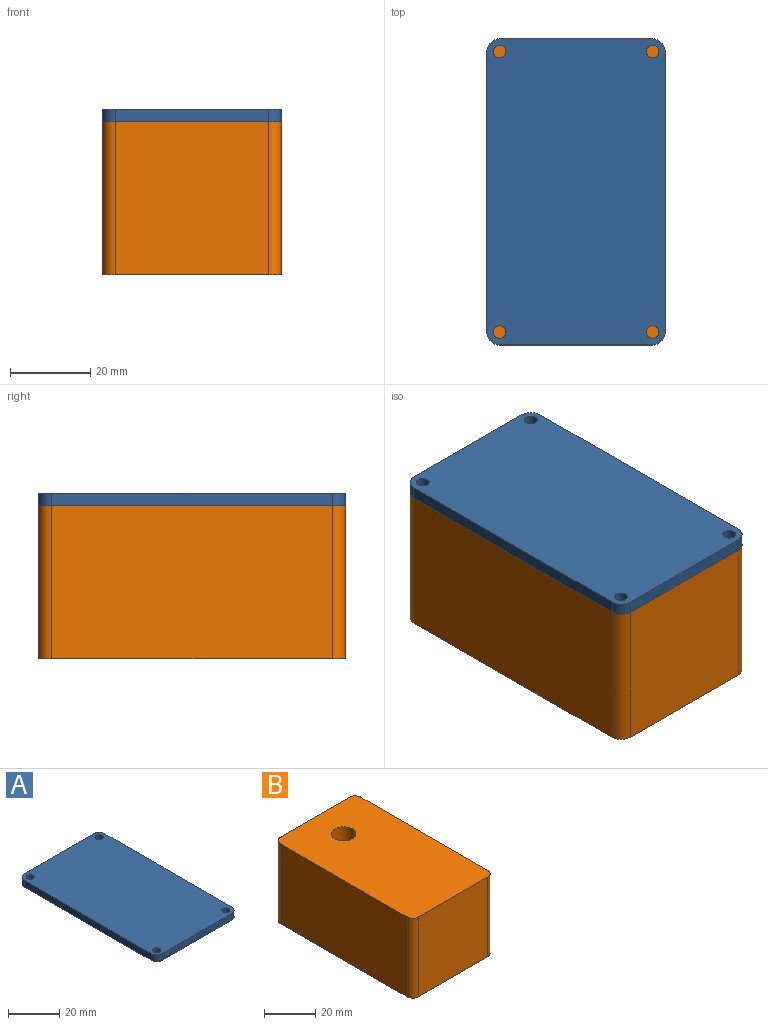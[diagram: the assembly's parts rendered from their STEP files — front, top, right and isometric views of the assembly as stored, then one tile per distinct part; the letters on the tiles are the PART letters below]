
ASSEMBLY  parts=2 mates=1
PART A: 14 faces, bbox 44.5x76.2x3.2 mm
  f0: plane 69.85x3.18mm, normal (1,0,0), area 221.8mm2, adj f1,f7,f8,f9
  f1: cylinder r=3.17mm len=3.18mm, axis (0,0,-1), area 15.8mm2, adj f0,f2,f8,f9
  f2: plane 38.1x3.18mm, normal (0,1,0), area 121mm2, adj f1,f3,f8,f9
  f3: cylinder r=3.17mm len=3.18mm, axis (0,0,-1), area 15.8mm2, adj f2,f4,f8,f9
  f4: plane 69.85x3.18mm, normal (-1,0,0), area 221.8mm2, adj f3,f5,f8,f9
  f5: cylinder r=3.17mm len=3.18mm, axis (0,0,-1), area 15.8mm2, adj f4,f6,f8,f9
  f6: plane 38.1x3.18mm, normal (0,-1,0), area 121mm2, adj f5,f7,f8,f9
  f7: cylinder r=3.17mm len=3.18mm, axis (0,0,-1), area 15.8mm2, adj f0,f6,f8,f9
  f8: plane 76.2x44.45mm, normal (0,0,1), area 3346.8mm2, adj f0,f1,f2,f3,f4,f5,f6,f7
  f9: plane 76.2x44.45mm, normal (0,0,-1), area 3346.8mm2, adj f0,f1,f2,f3,f4,f5,f6,f7
  f10: cylinder r=1.59mm len=3.18mm, axis (0,0,1), area 31.7mm2, adj f8,f9
  f11: cylinder r=1.59mm len=3.18mm, axis (0,0,1), area 31.7mm2, adj f8,f9
  f12: cylinder r=1.59mm len=3.18mm, axis (0,0,1), area 31.7mm2, adj f8,f9
  f13: cylinder r=1.59mm len=3.18mm, axis (0,0,1), area 31.7mm2, adj f8,f9
PART B: 20 faces, bbox 44.5x76.2x38.1 mm
  f0: plane 76.2x44.45mm, normal (0,0,-1), area 1371mm2, adj f1,f2,f3,f4,f5,f6,f7,f8
  f1: plane 69.85x38.1mm, normal (1,0,0), area 2661.3mm2, adj f0,f2,f8,f9
  f2: cylinder r=3.17mm len=38.1mm, axis (0,0,-1), area 190mm2, adj f0,f1,f3,f9
  f3: plane 38.1x38.1mm, normal (0,1,0), area 1451.6mm2, adj f0,f2,f4,f9
  f4: cylinder r=3.17mm len=38.1mm, axis (0,0,-1), area 190mm2, adj f0,f3,f5,f9
  f5: plane 69.85x38.1mm, normal (-1,0,0), area 2661.3mm2, adj f0,f4,f6,f9
  f6: cylinder r=3.17mm len=38.1mm, axis (0,0,-1), area 190mm2, adj f0,f5,f7,f9
  f7: plane 38.1x38.1mm, normal (0,-1,0), area 1451.6mm2, adj f0,f6,f8,f9
  f8: cylinder r=3.17mm len=38.1mm, axis (0,0,-1), area 190mm2, adj f0,f1,f7,f9
  f9: plane 76.2x44.45mm, normal (0,0,1), area 3307.2mm2, adj f1,f2,f3,f4,f5,f6,f7,f8
  f10: plane 31.75x25.4mm, normal (0,-1,0), area 806.5mm2, adj f0,f11,f17,f18
  f11: cylinder r=3.17mm len=31.75mm, axis (0,0,-1), area 158.3mm2, adj f0,f10,f12,f18
  f12: plane 57.15x31.75mm, normal (1,0,0), area 1814.5mm2, adj f0,f11,f13,f18
  f13: cylinder r=3.17mm len=31.75mm, axis (0,0,-1), area 158.3mm2, adj f0,f12,f14,f18
  f14: plane 31.75x25.4mm, normal (0,1,0), area 806.5mm2, adj f0,f13,f15,f18
  f15: cylinder r=3.17mm len=31.75mm, axis (0,0,-1), area 158.3mm2, adj f0,f14,f16,f18
  f16: plane 57.15x31.75mm, normal (-1,0,0), area 1814.5mm2, adj f0,f15,f17,f18
  f17: cylinder r=3.17mm len=31.75mm, axis (0,0,-1), area 158.3mm2, adj f0,f10,f16,f18
  f18: plane 63.5x31.75mm, normal (0,0,-1), area 1936.2mm2, adj f10,f11,f12,f13,f14,f15,f16,f17
  f19: cylinder r=4.76mm len=9.53mm, axis (0,0,-1), area 190mm2, adj f9,f18
PLACE A at identity fixed
PLACE B rot(axis=(1,0,0),180deg) t=(0,0,0)mm
MATE fastened B.f0 <-> A.f9  axis (0,0,1) through (0,0,0)mm
